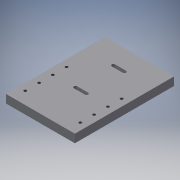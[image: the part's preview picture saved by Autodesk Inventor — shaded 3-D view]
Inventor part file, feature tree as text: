
AUTODESK INVENTOR PART (.ipt)
format: ipt  version: 2019 (Build 230136000, 136)  size: 182,784 bytes
history: native  units: mm
features: reference x8, sketch x4, extrude x3, plane x1, hole x1, projected_geometry x1
ambient origin geometry x8: Origin, YZ Plane, XZ Plane, XY Plane, X Axis, Y Axis, Z Axis, Center Point
bodies: Solid1 (feature_tree)
feature tree (18):
  sketch  "Sketch1"  dims[d0=180.0mm d1=125.0mm]
  plane  "Work Plane1"
  extrude  "Extrusion1"  Depth=125.0mm
  hole  "Hole1"  [1 undecoded]
  extrude  "Extrusion2"  Depth=7.0mm
  extrude  "Extrusion3"  Depth=3.0mm
  reference  "Reference1"
  reference  "Reference2"
  sketch  "Sketch2"  dims[d2=15.0mm d3=0.0mm d5=55.0mm]
  reference  "Reference3"
  reference  "Reference4"
  reference  "Reference5"
  reference  "Reference6"
  sketch  "Sketch4"  dims[d6=40.0mm d8=25.0mm d9=20.0mm d11=100.0mm]
  reference  "Reference7"
  reference  "Reference8"
  sketch  "Sketch5"  dims[d14=4.917mm d15=6.0mm d16=4.0mm d17=2.0mm d18=90.0deg d19=8.0mm d20=20.594885mm d21=20.0mm d22=3.0mm d23=3.0mm d24=6.0mm d25=15.0mm d26=0.0mm d27=47.5mm d28=20.0mm d30=68.866mm d31=10.0mm d33=10.0mm d35=12.0mm d36=6.0mm d37=6.0mm d38=6.0mm d39=20.0mm d41=68.866mm d42=10.0mm d44=10.0mm d46=7.0mm d47=0.0mm]
  projected_geometry  "Projected Loop1"
note: 1 required parameter value undecoded (feature->parameter linkage not recoverable at this tier; creation-order binding heuristic only, values carry confidence <= 0.55)
